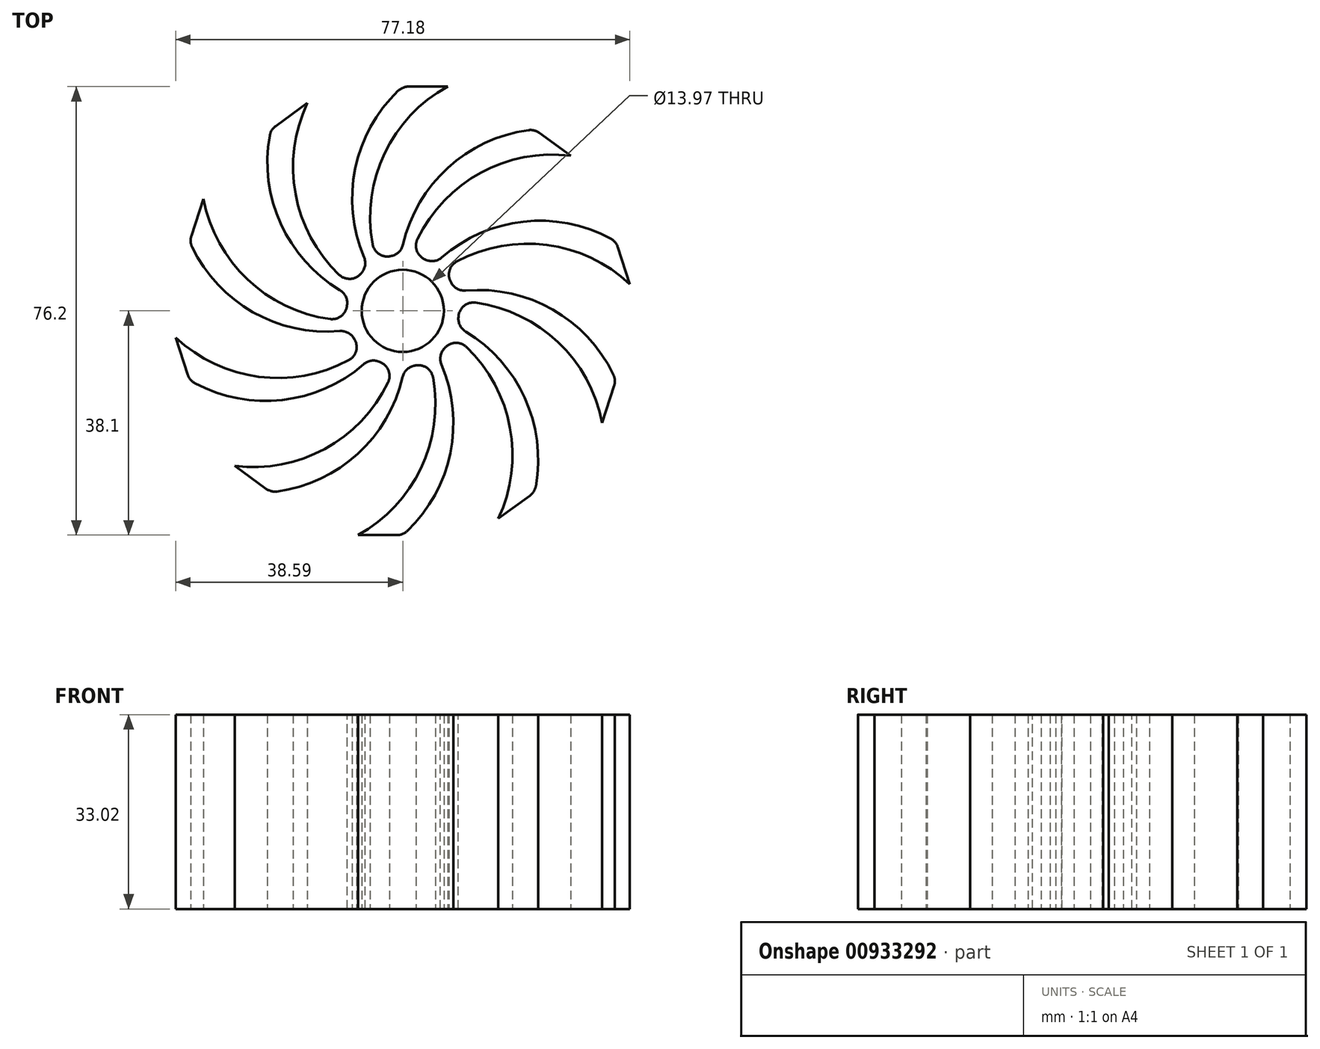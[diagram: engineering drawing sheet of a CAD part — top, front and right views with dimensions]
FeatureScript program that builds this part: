
annotation { "Feature Type Name" : "Feature", "Feature Type Description" : "" }
export const myFeature = defineFeature(function(context is Context, id is Id, definition is map)
    precondition{}
    {
        {
            var Q0;
            Q0=qCreatedBy(makeId("Top.planeOp"),FACE);
            var sketch = newSketch(context, id + "F0", { "sketchPlane" : qUnion([Q0])});
            skCircle(sketch, "E0", {"center": v(0, 0) * mm, "radius": 9.53 * mm});
            skArc(sketch, "E1", {"start": v(0, 38.1) * mm, "mid": v(-8.6, 19.05) * mm, "end": v(0, 0) * mm});
            skArc(sketch, "E2", {"start": v(7.62, 38.1) * mm, "mid": v(-5.05, 20.82) * mm, "end": v(0, 0) * mm});
            skLineSegment(sketch, "E3", {"start": v(0, 38.1) * mm, "end": v(7.62, 38.1) * mm});
            skLineSegment(sketch, "E4.1.0", {"start": v(-22.4, 30.82) * mm, "end": v(-16.23, 35.3) * mm});
            skArc(sketch, "E4.1.1", {"start": v(-16.23, 35.3) * mm, "mid": v(-16.33, 13.88) * mm, "end": v(0, 0) * mm});
            skArc(sketch, "E4.1.2", {"start": v(-22.4, 30.82) * mm, "mid": v(-18.15, 10.36) * mm, "end": v(0, 0) * mm});
            skLineSegment(sketch, "E4.2.0", {"start": v(-36.24, 11.77) * mm, "end": v(-33.88, 19.02) * mm});
            skArc(sketch, "E4.2.1", {"start": v(-33.88, 19.02) * mm, "mid": v(-21.36, 1.63) * mm, "end": v(0, 0) * mm});
            skArc(sketch, "E4.2.2", {"start": v(-36.24, 11.77) * mm, "mid": v(-20.78, -2.3) * mm, "end": v(0, 0) * mm});
            skLineSegment(sketch, "E4.3.0", {"start": v(-36.24, -11.77) * mm, "end": v(-38.59, -4.53) * mm});
            skArc(sketch, "E4.3.1", {"start": v(-38.59, -4.53) * mm, "mid": v(-18.24, -11.24) * mm, "end": v(0, 0) * mm});
            skArc(sketch, "E4.3.2", {"start": v(-36.24, -11.77) * mm, "mid": v(-15.46, -14.07) * mm, "end": v(0, 0) * mm});
            skLineSegment(sketch, "E4.4.0", {"start": v(-22.4, -30.82) * mm, "end": v(-28.56, -26.34) * mm});
            skArc(sketch, "E4.4.1", {"start": v(-28.56, -26.34) * mm, "mid": v(-8.15, -19.81) * mm, "end": v(0, 0) * mm});
            skArc(sketch, "E4.4.2", {"start": v(-22.4, -30.82) * mm, "mid": v(-4.24, -20.47) * mm, "end": v(0, 0) * mm});
            skLineSegment(sketch, "E4.5.0", {"start": v(0, -38.1) * mm, "end": v(-7.62, -38.1) * mm});
            skArc(sketch, "E4.5.1", {"start": v(-7.62, -38.1) * mm, "mid": v(5.05, -20.82) * mm, "end": v(0, 0) * mm});
            skArc(sketch, "E4.5.2", {"start": v(0, -38.1) * mm, "mid": v(8.6, -19.05) * mm, "end": v(0, 0) * mm});
            skLineSegment(sketch, "E4.6.0", {"start": v(22.4, -30.82) * mm, "end": v(16.23, -35.3) * mm});
            skArc(sketch, "E4.6.1", {"start": v(16.23, -35.3) * mm, "mid": v(16.33, -13.88) * mm, "end": v(0, 0) * mm});
            skArc(sketch, "E4.6.2", {"start": v(22.4, -30.82) * mm, "mid": v(18.15, -10.36) * mm, "end": v(0, 0) * mm});
            skLineSegment(sketch, "E4.7.0", {"start": v(36.24, -11.77) * mm, "end": v(33.88, -19.02) * mm});
            skArc(sketch, "E4.7.1", {"start": v(33.88, -19.02) * mm, "mid": v(21.36, -1.63) * mm, "end": v(0, 0) * mm});
            skArc(sketch, "E4.7.2", {"start": v(36.24, -11.77) * mm, "mid": v(20.78, 2.3) * mm, "end": v(0, 0) * mm});
            skLineSegment(sketch, "E4.8.0", {"start": v(36.24, 11.77) * mm, "end": v(38.59, 4.53) * mm});
            skArc(sketch, "E4.8.1", {"start": v(38.59, 4.53) * mm, "mid": v(18.24, 11.24) * mm, "end": v(0, 0) * mm});
            skArc(sketch, "E4.8.2", {"start": v(36.24, 11.77) * mm, "mid": v(15.46, 14.07) * mm, "end": v(0, 0) * mm});
            skLineSegment(sketch, "E4.9.0", {"start": v(22.4, 30.82) * mm, "end": v(28.56, 26.34) * mm});
            skArc(sketch, "E4.9.1", {"start": v(28.56, 26.34) * mm, "mid": v(8.15, 19.81) * mm, "end": v(0, 0) * mm});
            skArc(sketch, "E4.9.2", {"start": v(22.4, 30.82) * mm, "mid": v(4.24, 20.47) * mm, "end": v(0, 0) * mm});
            skSolve(sketch);
        }
        {
            var Q0;
            Q0 = qSketchRegion(id + "F0", true);
            extrude(context, id + "F1", {"entities" : qUnion([Q0]), "depth" : 33.02 * mm, "offsetDistance" : 25.4 * mm});
        }
        {
            var Q0;
            Q0=makeQuery(id+"F1.opExtrude","SWEPT_EDGE",EDGE,{"disambiguationData":[OSD([sQuery(id+"F0.wireOp",EDGE,"E4.1.0"),sQuery(id+"F0.wireOp",EDGE,"E4.1.2")])]});
            var Q1;
            Q1=makeQuery(id+"F1.opExtrude","SWEPT_EDGE",EDGE,{"disambiguationData":[OSD([sQuery(id+"F0.wireOp",EDGE,"E1"),sQuery(id+"F0.wireOp",EDGE,"E3")])]});
            var Q2;
            Q2=makeQuery(id+"F1.opExtrude","SWEPT_EDGE",EDGE,{"disambiguationData":[OSD([sQuery(id+"F0.wireOp",EDGE,"E4.2.0"),sQuery(id+"F0.wireOp",EDGE,"E4.2.2")])]});
            var Q3;
            Q3=makeQuery(id+"F1.opExtrude","SWEPT_EDGE",EDGE,{"disambiguationData":[OSD([sQuery(id+"F0.wireOp",EDGE,"E4.3.0"),sQuery(id+"F0.wireOp",EDGE,"E4.3.2")])]});
            var Q4;
            Q4=makeQuery(id+"F1.opExtrude","SWEPT_EDGE",EDGE,{"disambiguationData":[OSD([sQuery(id+"F0.wireOp",EDGE,"E4.4.0"),sQuery(id+"F0.wireOp",EDGE,"E4.4.2")])]});
            var Q5;
            Q5=makeQuery(id+"F1.opExtrude","SWEPT_EDGE",EDGE,{"disambiguationData":[OSD([sQuery(id+"F0.wireOp",EDGE,"E4.5.0"),sQuery(id+"F0.wireOp",EDGE,"E4.5.2")])]});
            var Q6;
            Q6=makeQuery(id+"F1.opExtrude","SWEPT_EDGE",EDGE,{"disambiguationData":[OSD([sQuery(id+"F0.wireOp",EDGE,"E4.6.0"),sQuery(id+"F0.wireOp",EDGE,"E4.6.2")])]});
            var Q7;
            Q7=makeQuery(id+"F1.opExtrude","SWEPT_EDGE",EDGE,{"disambiguationData":[OSD([sQuery(id+"F0.wireOp",EDGE,"E4.7.0"),sQuery(id+"F0.wireOp",EDGE,"E4.7.2")])]});
            var Q8;
            Q8=makeQuery(id+"F1.opExtrude","SWEPT_EDGE",EDGE,{"disambiguationData":[OSD([sQuery(id+"F0.wireOp",EDGE,"E4.8.0"),sQuery(id+"F0.wireOp",EDGE,"E4.8.2")])]});
            var Q9;
            Q9=makeQuery(id+"F1.opExtrude","SWEPT_EDGE",EDGE,{"disambiguationData":[OSD([sQuery(id+"F0.wireOp",EDGE,"E4.9.0"),sQuery(id+"F0.wireOp",EDGE,"E4.9.2")])]});
            var Q10;
            Q10=makeQuery(id+"F1.opExtrude","SWEPT_EDGE",EDGE,{"disambiguationData":[OSD([sQuery(id+"F0.wireOp",EDGE,"E0"),sQuery(id+"F0.wireOp",EDGE,"E2")])]});
            var Q11;
            Q11=makeQuery(id+"F1.opExtrude","SWEPT_EDGE",EDGE,{"disambiguationData":[OSD([sQuery(id+"F0.wireOp",EDGE,"E0"),sQuery(id+"F0.wireOp",EDGE,"E1")])]});
            var Q12;
            Q12=makeQuery(id+"F1.opExtrude","SWEPT_EDGE",EDGE,{"disambiguationData":[OSD([sQuery(id+"F0.wireOp",EDGE,"E0"),sQuery(id+"F0.wireOp",EDGE,"E4.1.1")])]});
            var Q13;
            Q13=makeQuery(id+"F1.opExtrude","SWEPT_EDGE",EDGE,{"disambiguationData":[OSD([sQuery(id+"F0.wireOp",EDGE,"E0"),sQuery(id+"F0.wireOp",EDGE,"E4.1.2")])]});
            var Q14;
            Q14=makeQuery(id+"F1.opExtrude","SWEPT_EDGE",EDGE,{"disambiguationData":[OSD([sQuery(id+"F0.wireOp",EDGE,"E0"),sQuery(id+"F0.wireOp",EDGE,"E4.2.1")])]});
            var Q15;
            Q15=makeQuery(id+"F1.opExtrude","SWEPT_EDGE",EDGE,{"disambiguationData":[OSD([sQuery(id+"F0.wireOp",EDGE,"E0"),sQuery(id+"F0.wireOp",EDGE,"E4.2.2")])]});
            var Q16;
            Q16=makeQuery(id+"F1.opExtrude","SWEPT_EDGE",EDGE,{"disambiguationData":[OSD([sQuery(id+"F0.wireOp",EDGE,"E0"),sQuery(id+"F0.wireOp",EDGE,"E4.3.1")])]});
            var Q17;
            Q17=makeQuery(id+"F1.opExtrude","SWEPT_EDGE",EDGE,{"disambiguationData":[OSD([sQuery(id+"F0.wireOp",EDGE,"E0"),sQuery(id+"F0.wireOp",EDGE,"E4.3.2")])]});
            var Q18;
            Q18=makeQuery(id+"F1.opExtrude","SWEPT_EDGE",EDGE,{"disambiguationData":[OSD([sQuery(id+"F0.wireOp",EDGE,"E0"),sQuery(id+"F0.wireOp",EDGE,"E4.4.1")])]});
            var Q19;
            Q19=makeQuery(id+"F1.opExtrude","SWEPT_EDGE",EDGE,{"disambiguationData":[OSD([sQuery(id+"F0.wireOp",EDGE,"E0"),sQuery(id+"F0.wireOp",EDGE,"E4.4.2")])]});
            var Q20;
            Q20=makeQuery(id+"F1.opExtrude","SWEPT_EDGE",EDGE,{"disambiguationData":[OSD([sQuery(id+"F0.wireOp",EDGE,"E0"),sQuery(id+"F0.wireOp",EDGE,"E4.5.1")])]});
            var Q21;
            Q21=makeQuery(id+"F1.opExtrude","SWEPT_EDGE",EDGE,{"disambiguationData":[OSD([sQuery(id+"F0.wireOp",EDGE,"E0"),sQuery(id+"F0.wireOp",EDGE,"E4.5.2")])]});
            var Q22;
            Q22=makeQuery(id+"F1.opExtrude","SWEPT_EDGE",EDGE,{"disambiguationData":[OSD([sQuery(id+"F0.wireOp",EDGE,"E0"),sQuery(id+"F0.wireOp",EDGE,"E4.6.1")])]});
            var Q23;
            Q23=makeQuery(id+"F1.opExtrude","SWEPT_EDGE",EDGE,{"disambiguationData":[OSD([sQuery(id+"F0.wireOp",EDGE,"E0"),sQuery(id+"F0.wireOp",EDGE,"E4.6.2")])]});
            var Q24;
            Q24=makeQuery(id+"F1.opExtrude","SWEPT_EDGE",EDGE,{"disambiguationData":[OSD([sQuery(id+"F0.wireOp",EDGE,"E0"),sQuery(id+"F0.wireOp",EDGE,"E4.7.1")])]});
            var Q25;
            Q25=makeQuery(id+"F1.opExtrude","SWEPT_EDGE",EDGE,{"disambiguationData":[OSD([sQuery(id+"F0.wireOp",EDGE,"E0"),sQuery(id+"F0.wireOp",EDGE,"E4.7.2")])]});
            var Q26;
            Q26=makeQuery(id+"F1.opExtrude","SWEPT_EDGE",EDGE,{"disambiguationData":[OSD([sQuery(id+"F0.wireOp",EDGE,"E0"),sQuery(id+"F0.wireOp",EDGE,"E4.8.1")])]});
            var Q27;
            Q27=makeQuery(id+"F1.opExtrude","SWEPT_EDGE",EDGE,{"disambiguationData":[OSD([sQuery(id+"F0.wireOp",EDGE,"E0"),sQuery(id+"F0.wireOp",EDGE,"E4.8.2")])]});
            var Q28;
            Q28=makeQuery(id+"F1.opExtrude","SWEPT_EDGE",EDGE,{"disambiguationData":[OSD([sQuery(id+"F0.wireOp",EDGE,"E0"),sQuery(id+"F0.wireOp",EDGE,"E4.9.1")])]});
            var Q29;
            Q29=makeQuery(id+"F1.opExtrude","SWEPT_EDGE",EDGE,{"disambiguationData":[OSD([sQuery(id+"F0.wireOp",EDGE,"E0"),sQuery(id+"F0.wireOp",EDGE,"E4.9.2")])]});
            fillet(context, id + "F2", {"entities" : qUnion([Q0, Q1, Q2, Q3, Q4, Q5, Q6, Q7, Q8, Q9, Q10, Q11, Q12, Q13, Q14, Q15, Q16, Q17, Q18, Q19, Q20, Q21, Q22, Q23, Q24, Q25, Q26, Q27, Q28, Q29]), "radius" : 2.54 * mm, "tangentPropagation" : true, "allowEdgeOverflow" : false});
        }
        {
            var Q0;
            Q0=qCreatedBy(makeId("Top.planeOp"),FACE);
            var sketch = newSketch(context, id + "F3", { "sketchPlane" : qUnion([Q0])});
            skCircle(sketch, "E5", {"center": v(0, 0) * mm, "radius": 6.99 * mm});
            skSolve(sketch);
        }
        {
            var Q0;
            Q0 = qSketchRegion(id + "F3", true);
            extrude(context, id + "F4", {"entities" : qUnion([Q0]), "operationType" : NewBodyOperationType.REMOVE, "endBound" : BoundingType.THROUGH_ALL, "depth" : 25.4 * mm, "offsetDistance" : 25.4 * mm});
        }
    });
